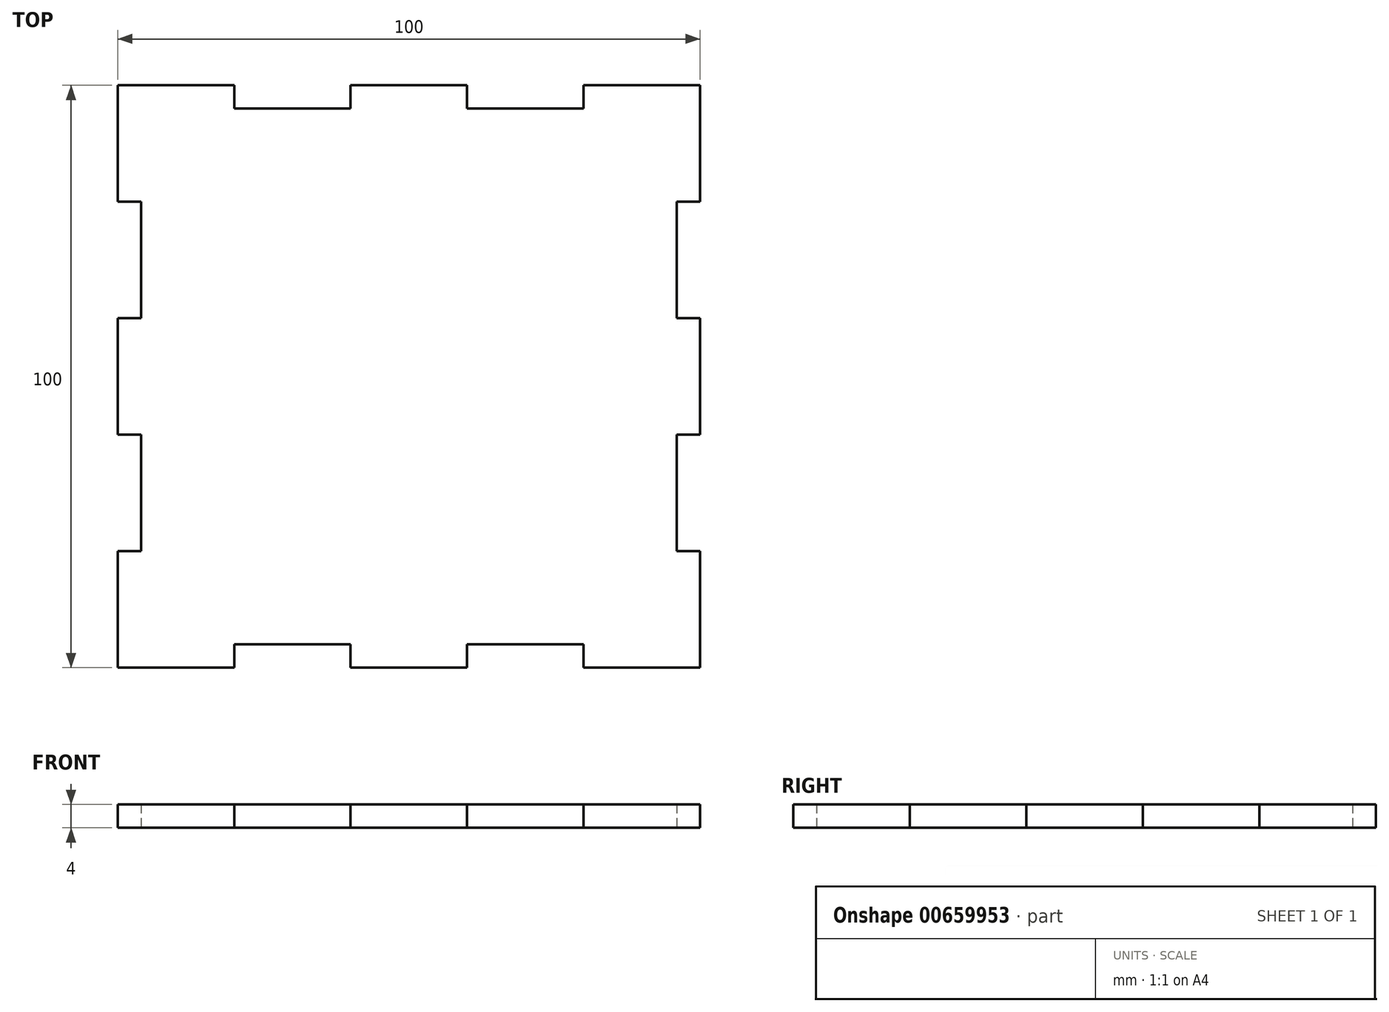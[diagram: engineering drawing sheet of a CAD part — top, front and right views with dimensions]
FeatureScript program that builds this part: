
annotation { "Feature Type Name" : "Feature", "Feature Type Description" : "" }
export const myFeature = defineFeature(function(context is Context, id is Id, definition is map)
    precondition{}
    {
        {
            var Q0;
            Q0=qCreatedBy(makeId("Top.planeOp"),FACE);
            var sketch = newSketch(context, id + "F0", { "sketchPlane" : qUnion([Q0])});
            skLineSegment(sketch, "E0.bottom", {"start": v(-30.45, 80) * mm, "end": v(69.55, 80) * mm});
            skLineSegment(sketch, "E0.top", {"start": v(-30.45, -20) * mm, "end": v(69.55, -20) * mm});
            skLineSegment(sketch, "E0.left", {"start": v(-30.45, 80) * mm, "end": v(-30.45, -20) * mm});
            skLineSegment(sketch, "E0.right", {"start": v(69.55, 80) * mm, "end": v(69.55, -20) * mm});
            skLineSegment(sketch, "E1.bottom", {"start": v(-10.45, -20) * mm, "end": v(9.55, -20) * mm});
            skLineSegment(sketch, "E1.top", {"start": v(-10.45, -16) * mm, "end": v(9.55, -16) * mm});
            skLineSegment(sketch, "E1.left", {"start": v(-10.45, -20) * mm, "end": v(-10.45, -16) * mm});
            skLineSegment(sketch, "E1.right", {"start": v(9.55, -20) * mm, "end": v(9.55, -16) * mm});
            skLineSegment(sketch, "E2.bottom", {"start": v(29.55, -20) * mm, "end": v(49.55, -20) * mm});
            skLineSegment(sketch, "E2.top", {"start": v(29.55, -16) * mm, "end": v(49.55, -16) * mm});
            skLineSegment(sketch, "E2.left", {"start": v(29.55, -20) * mm, "end": v(29.55, -16) * mm});
            skLineSegment(sketch, "E2.right", {"start": v(49.55, -20) * mm, "end": v(49.55, -16) * mm});
            skLineSegment(sketch, "E3.bottom", {"start": v(-10.45, 80) * mm, "end": v(9.55, 80) * mm});
            skLineSegment(sketch, "E3.top", {"start": v(-10.45, 76) * mm, "end": v(9.55, 76) * mm});
            skLineSegment(sketch, "E3.left", {"start": v(-10.45, 80) * mm, "end": v(-10.45, 76) * mm});
            skLineSegment(sketch, "E3.right", {"start": v(9.55, 80) * mm, "end": v(9.55, 76) * mm});
            skLineSegment(sketch, "E4.bottom", {"start": v(29.55, 80) * mm, "end": v(49.55, 80) * mm});
            skLineSegment(sketch, "E4.top", {"start": v(29.55, 76) * mm, "end": v(49.55, 76) * mm});
            skLineSegment(sketch, "E4.left", {"start": v(29.55, 80) * mm, "end": v(29.55, 76) * mm});
            skLineSegment(sketch, "E4.right", {"start": v(49.55, 80) * mm, "end": v(49.55, 76) * mm});
            skLineSegment(sketch, "E5.bottom", {"start": v(-30.45, 60) * mm, "end": v(-26.45, 60) * mm});
            skLineSegment(sketch, "E5.top", {"start": v(-30.45, 40) * mm, "end": v(-26.45, 40) * mm});
            skLineSegment(sketch, "E5.left", {"start": v(-30.45, 60) * mm, "end": v(-30.45, 40) * mm});
            skLineSegment(sketch, "E5.right", {"start": v(-26.45, 60) * mm, "end": v(-26.45, 40) * mm});
            skLineSegment(sketch, "E6.bottom", {"start": v(-30.45, 20) * mm, "end": v(-26.45, 20) * mm});
            skLineSegment(sketch, "E6.top", {"start": v(-30.45, 0) * mm, "end": v(-26.45, 0) * mm});
            skLineSegment(sketch, "E6.left", {"start": v(-30.45, 20) * mm, "end": v(-30.45, 0) * mm});
            skLineSegment(sketch, "E6.right", {"start": v(-26.45, 20) * mm, "end": v(-26.45, 0) * mm});
            skLineSegment(sketch, "E7.bottom", {"start": v(69.55, 60) * mm, "end": v(65.55, 60) * mm});
            skLineSegment(sketch, "E7.top", {"start": v(69.55, 40) * mm, "end": v(65.55, 40) * mm});
            skLineSegment(sketch, "E7.left", {"start": v(69.55, 60) * mm, "end": v(69.55, 40) * mm});
            skLineSegment(sketch, "E7.right", {"start": v(65.55, 60) * mm, "end": v(65.55, 40) * mm});
            skLineSegment(sketch, "E8.bottom", {"start": v(69.55, 20) * mm, "end": v(65.55, 20) * mm});
            skLineSegment(sketch, "E8.top", {"start": v(69.55, 0) * mm, "end": v(65.55, 0) * mm});
            skLineSegment(sketch, "E8.left", {"start": v(69.55, 20) * mm, "end": v(69.55, 0) * mm});
            skLineSegment(sketch, "E8.right", {"start": v(65.55, 20) * mm, "end": v(65.55, 0) * mm});
            skSolve(sketch);
        }
        {
            var Q0;
            Q0=makeQuery(id+"F0.imprint","IMPRINT",FACE,{"disambiguationData":[TD([[makeQuery(id+"F0.imprint","IMPRINT",EDGE,{"derivedFrom":sQuery(id+"F0.wireOp",EDGE,"E1.top")}),1.0]])]});
            extrude(context, id + "F1", {"entities" : qUnion([Q0]), "depth" : 4 * mm, "offsetDistance" : 25 * mm});
        }
    });
